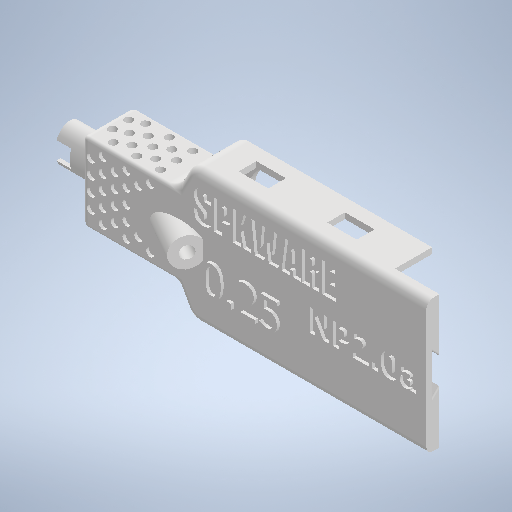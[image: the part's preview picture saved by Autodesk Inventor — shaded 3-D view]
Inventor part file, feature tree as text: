
AUTODESK INVENTOR PART (.ipt)
format: ipt  version: 2025 (Build 290162000, 162)  size: 1,398,272 bytes
history: native  units: in
note: dims shown in document units (in); Inventor stores cm internally (conversion verified against a paired STEP export)
features: extrude x21, reference x13, other x12, fillet x11, sketch x6, plane x1, loft x1
ambient origin geometry x8: Origin, YZ Plane, XZ Plane, XY Plane, X Axis, Y Axis, Z Axis, Center Point
bodies: Solid1 (feature_tree)
feature tree (65):
  extrude  "dovetail_base"  Depth=0.0031in
  extrude  "tip_offset"  Depth=0.1772in
  extrude  "enclosure_proximal"  Depth=0.0354in
  extrude  "enclosure_front"  Depth=0.8858in TaperAngle=0.0deg
  extrude  "tip_opening"  Depth=0.1339in
  extrude  "tip_enclosure"  Depth=0.0157in
  extrude  "tip_sealing"  Depth=0.0157in
  other  "screw_planeheight"
  other  "screw_workplane"
  extrude  "screw_support"  Depth=0.2362in TaperAngle=0.0deg
  extrude  "screw_hole"  Depth=0.0157in TaperAngle=0.0deg
  extrude  "cement_aid_front"  Depth=0.3268in
  extrude  "cement_aid_back"  TaperAngle=120.0deg  [1 undecoded]
  extrude  "cement_aid_left"  Depth=0.0787in
  extrude  "cement_aid_right"  Depth=0.0315in
  plane  "Work Plane5"
  extrude  "top_enclosure"  Depth=1.0in TaperAngle=0.0deg
  loft  "Loft1"
  extrude  "flex_holder"  Depth=0.0315in
  extrude  "top_side_cover"  Depth=1.0in TaperAngle=0.0deg
  fillet  "Fillet6"  Radius=0.0335in
  fillet  "Fillet7"  Radius=0.0512in
  fillet  "Fillet8"  Radius=0.0394in
  extrude  "cover_holes"  Depth=1.0in TaperAngle=0.0deg
  fillet  "Fillet9"  Radius=0.0276in
  fillet  "Fillet10"  Radius=0.0472in
  fillet  "Fillet12"  Radius=0.0984in
  fillet  "Fillet13"  Radius=0.0472in
  fillet  "Fillet14"  Radius=0.0236in
  extrude  "bottom_tolerance"  Depth=0.0394in TaperAngle=0.0deg
  fillet  "Fillet15"  Radius=0.0217in
  fillet  "Fillet16"  Radius=0.0394in
  fillet  "Fillet17"  Radius=0.0394in
  extrude  "Extrusion25"  Depth=0.0394in
  extrude  "text_tol"  Depth=0.0217in
  reference  "Reference1"
  reference  "Reference2"
  reference  "Reference3"
  reference  "Reference4"
  reference  "Reference5"
  reference  "Reference6"
  reference  "Reference7"
  reference  "Reference8"
  reference  "Reference9"
  reference  "Reference10"
  reference  "Reference11"
  reference  "Reference12"
  reference  "Reference13"
  sketch  "Sketch9"  dims[d6=0.0004in d7=0.0031in]
  sketch  "Sketch10"  dims[d8=0.0098in d10=0.1772in]
  sketch  "Sketch12"  dims[d11=0.1378in d12=0.0354in]
  sketch  "Sketch13"  dims[d13=0.0in d14=0.8858in d15=0.0in]
  sketch  "Sketch15"  dims[d16=0.0197in d17=0.0in d18=0.1339in]
  other  "Edges1"
  other  "Edges2"
  sketch  "Sketch26"  dims[d19=0.0157in d20=0.0157in d21=0.0157in d22=0.2362in d23=0.0in d24=0.0157in d25=0.0in d82=0.3268in d83=120.0deg d84=0.0787in d87=0.0315in d88=1.0in d89=0.0in d90=0.0335in d91=0.0315in d92=1.0in d93=0.0in d94=0.0335in d95=0.0512in d96=0.0394in d97=1.0in d98=0.0in d99=0.0276in d100=0.0472in d101=0.0984in d102=0.0in d103=0.0472in d104=0.0236in d105=0.0394in d106=0.0in d107=0.0217in d108=0.0394in d109=0.0394in d110=0.0394in d114=0.0217in d115=0.0394in d117=0.0394in d118=0.0394in d123=0.0197in d126=0.0394in d128=0.0394in d129=0.0394in d130=0.0394in d137=0.0394in d141=0.0315in d142=0.0276in d143=0.0315in d144=0.0217in d145=0.0394in d153=1.0in d154=0.0in d155=0.0079in d156=0.0in d157=0.0315in d162=0.0433in d163=0.0433in d166=0.0433in d167=0.0433in d171=0.0433in d174=0.0236in d175=0.0315in d176=0.0315in d179=0.0433in d180=0.0433in d182=0.0315in d183=0.0236in d184=0.0118in d185=0.0in d186=1.0in d187=0.0in d188=0.0787in d189=0.0157in d190=0.0157in d191=0.0157in d192=0.3543in d193=0.1772in d194=0.0394in d195=0.0in d196=0.0in d197=90.0deg d198=0.0in d199=90.0deg d201=0.2205in d202=0.1102in d205=0.0394in d206=0.0in d207=0.5512in d208=0.0in d211=0.0197in d238=0.0315in d239=0.0827in d241=0.0079in d242=0.0315in d243=0.0315in d244=0.0787in d245=0.0787in d246=0.0472in d247=0.0591in d248=0.1575in d249=0.1181in d250=0.1575in d252=0.5118in d253=0.0in d254=0.0197in d255=0.0079in d257=0.0118in d259=0.0197in d261=0.0118in d262=0.0in d263=0.0in d266=0.0in d267=0.5906in d268=0.0in d269=0.0039in d271=0.0197in d274=0.0197in d275=0.0118in d9=0.0098in d277=0.0295in d278=0.1181in d279=0.0394in d280=0.0394in d281=0.0394in d282=0.0394in d289=0.0315in d291=0.0217in d292=0.0433in d293=0.0433in d294=0.0217in d295=0.0433in d296=0.0433in d297=0.0433in d298=0.0433in d300=0.0315in d301=0.0315in d302=0.0433in d303=0.0394in d304=0.0394in d305=0.0394in d306=0.0276in d307=0.0787in d309=0.0118in d310=0.0079in d311=0.0in d312=0.0079in d313=0.0in d314=0.0394in d315=0.0in d264=0.0in d265=0.0in]
  other  "text_sketch"
  other  "<userpath>\lib\np_holder\NP2a\full.iam"
  other  "full.iam"
  other  "Neuropixels_20_metal cap_NPM_FLEX_01-01-009:1"
  other  "U100_60"
  other  "J009777_NEUROPIXELS_DOVE_TAIL_MOUNT_GEN_2_NARROW_Rev_D_7"
  other  "Board_4"
  other  "Open CASCADE STEP translator 6.8 1.1.2_2"
  extrude  "Extruded_55"  Depth=0.0197in
note: 1 required parameter value undecoded (feature->parameter linkage not recoverable at this tier; creation-order binding heuristic only, values carry confidence <= 0.55)
